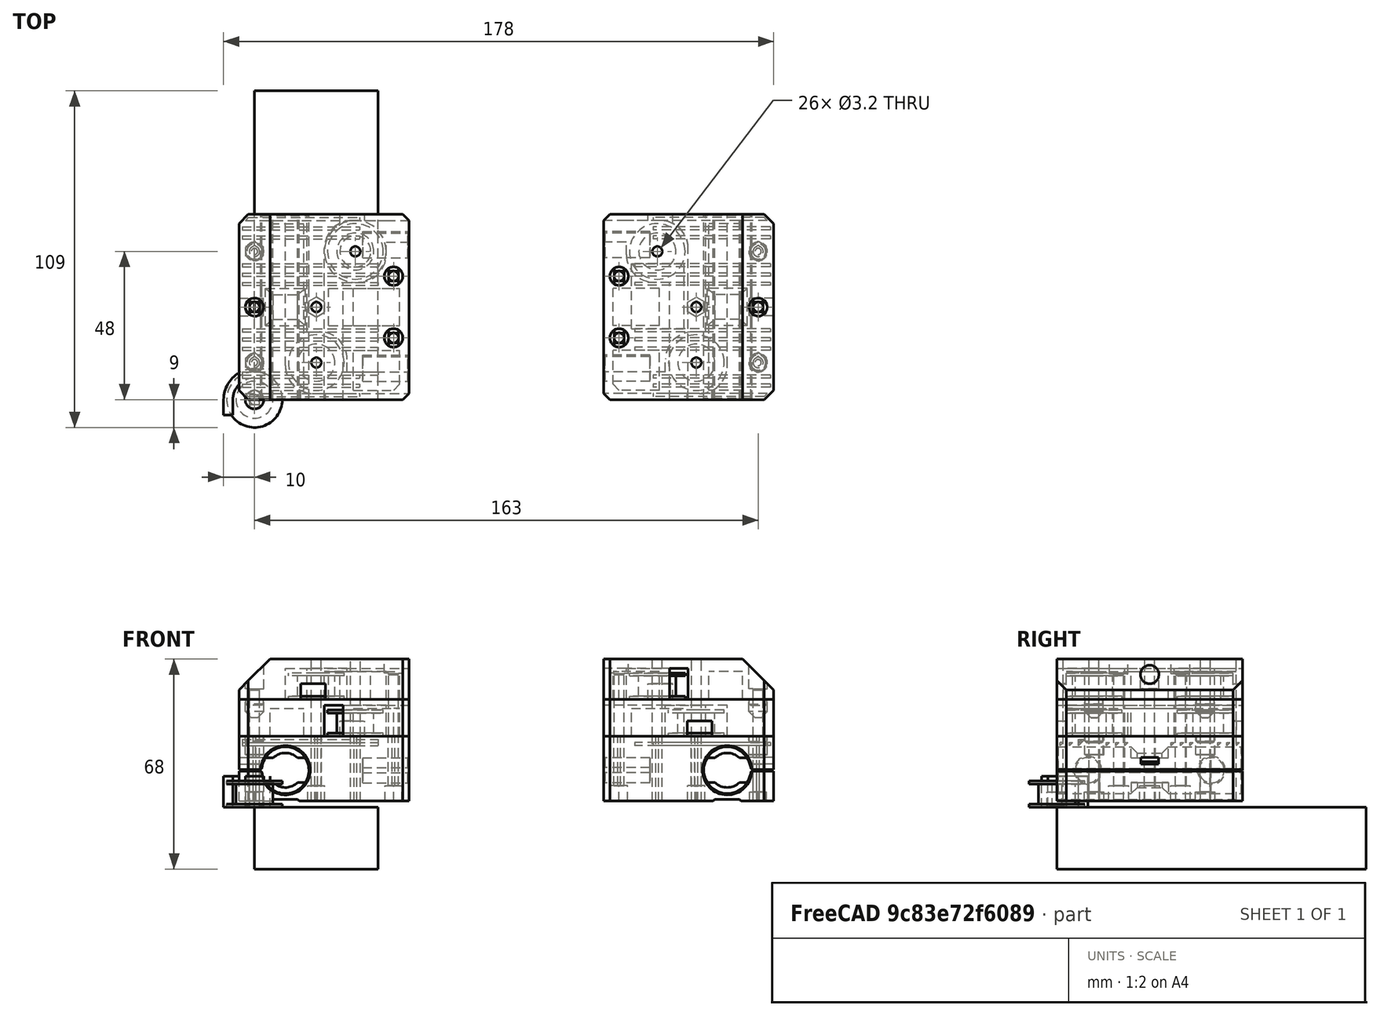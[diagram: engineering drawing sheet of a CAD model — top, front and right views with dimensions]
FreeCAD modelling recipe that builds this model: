
FCSTD DOCUMENT  (FreeCAD 0.18R14555 (Git shallow))
Label: Y-carrier
License: All rights reserved
LicenseURL: http://en.wikipedia.org/wiki/All_rights_reserved
objects: Part::Cylinder×59, Part::MultiFuse×41, Part::Box×39, Part::Cut×37, Part::Feature×29, Part::Chamfer×24, Part::MultiCommon×2, Part::Fillet×2
note: 233 computed .brp shape members not serialized (recipe doc carries the construction recipe); baked Part::Feature solids carry a one-line shape summary decoded from their .brp

FEATURE [Part::Box] Box  label="profile"
  AttacherType = Attacher::AttachEngine3D
  Height = 20
  Length = 40
  Placement = pos=(0,0,-20) rot=(0,0,1;0rad)
  Width = 100
FEATURE [Part::Cylinder] Cylinder  label="bushing-1"
  Angle = 360
  AttacherType = Attacher::AttachEngine3D
  Height = 24
  Placement = pos=(10,3e-15,12) rot=(-1,0,0;1.5708rad)
  Radius = 7.6
FEATURE [Part::Cylinder] Cylinder001  label="bushing-2"
  Angle = 360
  AttacherType = Attacher::AttachEngine3D
  Height = 24
  Placement = pos=(10,36,12) rot=(-1,0,0;1.5708rad)
  Radius = 7.6
FEATURE [Part::Cylinder] Cylinder002  label="rod"
  Angle = 360
  AttacherType = Attacher::AttachEngine3D
  Height = 100
  Placement = pos=(10,3e-15,12) rot=(-1,0,0;1.5708rad)
  Radius = 5.6
FEATURE [Part::Cylinder] Cylinder003  label="Cylinder"
  Angle = 360
  AttacherType = Attacher::AttachEngine3D
  Height = 30
  Placement = pos=(20,48,0) rot=(0,0,1;0rad)
  Radius = 1.6
FEATURE [Part::Cylinder] Cylinder004  label="Cylinder001-12.63"
  Angle = 360
  AttacherType = Attacher::AttachEngine3D
  Height = 30
  Placement = pos=(32.63,12,0) rot=(0,0,1;0rad)
  Radius = 1.6
FEATURE [Part::Box] Box001  label="Cube"
  AttacherType = Attacher::AttachEngine3D
  Height = 21
  Length = 55
  Placement = pos=(-5,0,2) rot=(0,0,1;0rad)
  Width = 60
FEATURE [Part::Cylinder] Cylinder005  label="Cylinder001"
  Angle = 360
  AttacherType = Attacher::AttachEngine3D
  Height = 1
  Radius = 9
FEATURE [Part::Cylinder] Cylinder006  label="Cylinder002"
  Angle = 360
  AttacherType = Attacher::AttachEngine3D
  Height = 1
  Placement = pos=(0,0,7.5) rot=(0,0,1;0rad)
  Radius = 9
FEATURE [Part::Cylinder] Cylinder007  label="Cylinder003"
  Angle = 360
  AttacherType = Attacher::AttachEngine3D
  Height = 8.5
  Radius = 6
FEATURE [Part::Cylinder] Cylinder008  label="Cylinder004"
  Angle = 360
  AttacherType = Attacher::AttachEngine3D
  Height = 8.5
  Radius = 1.6
FEATURE [Part::MultiFuse] Fusion
  Shapes = -> [Cylinder007,Cylinder006,Cylinder005]
FEATURE [Part::Cut] Cut  label="idler"
  Base = -> Fusion
  Tool = -> Cylinder008
FEATURE [Part::Feature] Cut001  label="idler001"
  Placement = pos=(20,12,35) rot=(0,0,1;0rad)
  shape: bbox 18 x 18 x 8.5 mm, 8 faces (baked)
FEATURE [Part::Feature] Cut002  label="idler002"
  Placement = pos=(32.63,48,23) rot=(0,0,1;0rad)
  shape: bbox 18 x 18 x 8.5 mm, 8 faces (baked)
FEATURE [Part::Cylinder] Cylinder009  label="Cylinder005"
  Angle = 360
  AttacherType = Attacher::AttachEngine3D
  Height = 20
  Placement = pos=(35,10,12) rot=(0,1,0;1.5708rad)
  Radius = 1
FEATURE [Part::Cylinder] Cylinder010  label="Cylinder006"
  Angle = 360
  AttacherType = Attacher::AttachEngine3D
  Height = 20
  Placement = pos=(35,50,12) rot=(0,1,0;1.5708rad)
  Radius = 1
FEATURE [Part::Cylinder] Cylinder011  label="Cylinder007"
  Angle = 360
  AttacherType = Attacher::AttachEngine3D
  Height = 30
  Placement = pos=(0,31.4,0) rot=(0,0,1;0rad)
  Radius = 0.5
FEATURE [Part::Cylinder] Cylinder012  label="Cylinder008"
  Angle = 360
  AttacherType = Attacher::AttachEngine3D
  Height = 30
  Placement = pos=(20,30,0) rot=(0,0,1;0rad)
  Radius = 1.65
FEATURE [Part::Cylinder] Cylinder014  label="Cylinder010"
  Angle = 360
  AttacherType = Attacher::AttachEngine3D
  Height = 30
  Placement = pos=(45,41.4,0) rot=(0,0,1;0rad)
  Radius = 0.5
FEATURE [Part::Cylinder] Cylinder015  label="Cylinder011"
  Angle = 360
  AttacherType = Attacher::AttachEngine3D
  Height = 6
  Placement = pos=(0,48,0) rot=(0,0,1;0rad)
  Radius = 3
FEATURE [Part::Cylinder] Cylinder016  label="Cylinder012"
  Angle = 360
  AttacherType = Attacher::AttachEngine3D
  Height = 6
  Placement = pos=(0,12,0) rot=(0,0,1;0rad)
  Radius = 3
FEATURE [Part::MultiFuse] Fusion001
  Shapes = -> [Cylinder002,Cylinder,Cylinder001]
FEATURE [Part::Box] Box002  label="Cube001"
  AttacherType = Attacher::AttachEngine3D
  Height = 0.5
  Length = 15
  Placement = pos=(-5,0,11.75) rot=(0,0,1;0rad)
  Width = 60
FEATURE [Part::Feature] Body001  label="hex-nut"
  shape: bbox 5.543 x 6.4 x 5 mm, 8 faces (baked)
FEATURE [Part::Feature] Body001001  label="hex-nut001"
  Placement = pos=(0,48,0) rot=(0,0,1;0rad)
  shape: bbox 5.543 x 6.4 x 5 mm, 8 faces (baked)
FEATURE [Part::Feature] Body001002  label="hex-nut002"
  Placement = pos=(0,12,0) rot=(0,0,1;0rad)
  shape: bbox 5.543 x 6.4 x 5 mm, 8 faces (baked)
FEATURE [Part::Cylinder] Cylinder017  label="Cylinder013"
  Angle = 360
  AttacherType = Attacher::AttachEngine3D
  Height = 30
  Placement = pos=(0,48,0) rot=(0,0,1;0rad)
  Radius = 0.5
FEATURE [Part::Cylinder] Cylinder018  label="Cylinder014"
  Angle = 360
  AttacherType = Attacher::AttachEngine3D
  Height = 30
  Placement = pos=(0,12,0) rot=(0,0,1;0rad)
  Radius = 0.5
FEATURE [Part::Cylinder] Cylinder019  label="Cylinder015"
  Angle = 360
  AttacherType = Attacher::AttachEngine3D
  Height = 30
  Placement = pos=(0,12,0) rot=(0,0,1;0rad)
  Radius = 1.65
FEATURE [Part::Cylinder] Cylinder020  label="Cylinder016"
  Angle = 360
  AttacherType = Attacher::AttachEngine3D
  Height = 30
  Placement = pos=(0,48,0) rot=(0,0,1;0rad)
  Radius = 1.65
FEATURE [Part::MultiFuse] Fusion003002
  Placement = pos=(0,1.4,0) rot=(0,0,1;0rad)
  Shapes = -> [Cylinder018,Cylinder017]
FEATURE [Part::Cylinder] Cylinder021  label="Cylinder017"
  Angle = 360
  AttacherType = Attacher::AttachEngine3D
  Height = 6
  Placement = pos=(0,12,0) rot=(0,0,1;0rad)
  Radius = 0.5
FEATURE [Part::Cylinder] Cylinder022  label="Cylinder018"
  Angle = 360
  AttacherType = Attacher::AttachEngine3D
  Height = 6
  Placement = pos=(0,48,0) rot=(0,0,1;0rad)
  Radius = 0.5
FEATURE [Part::Box] Box003  label="Cube002"
  AttacherType = Attacher::AttachEngine3D
  Height = 2.2
  Length = 8.8
  Placement = pos=(-5.9,27.1,14) rot=(0,0,1;0rad)
  Width = 5.8
FEATURE [Part::Feature] Body001003  label="hex-nut003"
  Placement = pos=(20,30,2) rot=(0,0,1;0rad)
  shape: bbox 5.543 x 6.4 x 5 mm, 8 faces (baked)
FEATURE [Part::Feature] Body001004  label="hex-nut004"
  Placement = pos=(45,40,2) rot=(0,0,1;0rad)
  shape: bbox 5.543 x 6.4 x 5 mm, 8 faces (baked)
FEATURE [Part::Cylinder] Cylinder023  label="Cylinder019"
  Angle = 360
  AttacherType = Attacher::AttachEngine3D
  Height = 30
  Placement = pos=(45,21.4,0) rot=(0,0,1;0rad)
  Radius = 0.5
FEATURE [Part::Feature] Body001005  label="hex-nut005"
  Placement = pos=(45,20,2) rot=(0,0,1;0rad)
  shape: bbox 5.543 x 6.4 x 5 mm, 8 faces (baked)
FEATURE [Part::Cylinder] Cylinder024  label="Cylinder020"
  Angle = 360
  AttacherType = Attacher::AttachEngine3D
  Height = 20
  Placement = pos=(35,10,12) rot=(0,1,0;1.5708rad)
  Radius = 4.075
FEATURE [Part::Cylinder] Cylinder025  label="Cylinder021"
  Angle = 360
  AttacherType = Attacher::AttachEngine3D
  Height = 20
  Placement = pos=(35,50,12) rot=(0,1,0;1.5708rad)
  Radius = 4.075
FEATURE [Part::MultiFuse] Fusion003006
  Shapes = -> [Cylinder024,Cylinder025]
FEATURE [Part::Cylinder] Cylinder026  label="Cylinder022"
  Angle = 360
  AttacherType = Attacher::AttachEngine3D
  Height = 30
  Placement = pos=(0,30,0) rot=(0,0,1;0rad)
  Radius = 1.65
FEATURE [Part::Cylinder] Cylinder027  label="Cylinder023"
  Angle = 360
  AttacherType = Attacher::AttachEngine3D
  Height = 30
  Placement = pos=(45,20,0) rot=(0,0,1;0rad)
  Radius = 1.65
FEATURE [Part::Cylinder] Cylinder028  label="Cylinder024"
  Angle = 360
  AttacherType = Attacher::AttachEngine3D
  Height = 30
  Placement = pos=(45,40,0) rot=(0,0,1;0rad)
  Radius = 1.65
FEATURE [Part::MultiFuse] Fusion003008
  Shapes = -> [Cylinder027,Cylinder023]
FEATURE [Part::MultiFuse] Fusion003009
  Shapes = -> [Cylinder014,Cylinder028]
FEATURE [Part::MultiFuse] Fusion003010
  Shapes = -> [Cylinder011,Cylinder026]
FEATURE [Part::Cylinder] Cylinder029  label="Cylinder025"
  Angle = 360
  AttacherType = Attacher::AttachEngine3D
  Height = 30
  Placement = pos=(20,31.4,0) rot=(0,0,1;0rad)
  Radius = 0.5
FEATURE [Part::MultiFuse] Fusion003011
  Shapes = -> [Cylinder012,Cylinder029]
FEATURE [Part::MultiFuse] Fusion003012
  Placement = pos=(0,3.4,0) rot=(0,0,1;0rad)
  Shapes = -> [Cylinder009,Cylinder010]
FEATURE [Part::Cylinder] Cylinder030  label="Cylinder001-12.064"
  Angle = 360
  AttacherType = Attacher::AttachEngine3D
  Height = 30
  Placement = pos=(32.63,13.3,0) rot=(0,0,1;0rad)
  Radius = 0.5
FEATURE [Part::Cylinder] Cylinder031  label="Cylinder026"
  Angle = 360
  AttacherType = Attacher::AttachEngine3D
  Height = 30
  Placement = pos=(20,49.3,0) rot=(0,0,1;0rad)
  Radius = 0.5
FEATURE [Part::MultiFuse] Fusion003015
  Shapes = -> [Fusion003011,Body001003]
FEATURE [Part::MultiFuse] Fusion003016
  Shapes = -> [Fusion003008,Body001005]
FEATURE [Part::MultiFuse] Fusion003017
  Shapes = -> [Fusion003009,Body001004]
FEATURE [Part::Box] Box004  label="Cube003"
  AttacherType = Attacher::AttachEngine3D
  Height = 3
  Length = 10
  Placement = pos=(5,0,0) rot=(0,0,1;0rad)
  Width = 60
FEATURE [Part::Chamfer] Chamfer003
  Base = -> Box004
  Edges = 2 edges r=1: [Edge2,Edge6]
  Placement = pos=(0,0,-0.5) rot=(0,0,1;0rad)
FEATURE [Part::Cylinder] Cylinder032  label="Cylinder027"
  Angle = 360
  AttacherType = Attacher::AttachEngine3D
  Height = 12
  Placement = pos=(10,24,12) rot=(-1,0,0;1.5708rad)
  Radius = 7.6
FEATURE [Part::Box] Box005  label="Cube004"
  AttacherType = Attacher::AttachEngine3D
  Height = 8
  Length = 16
  Placement = pos=(2,24,8) rot=(0,0,1;0rad)
  Width = 12
FEATURE [Part::MultiCommon] Common
  Shapes = -> [Cylinder032,Box005]
FEATURE [Part::Cut] Cut003
  Base = -> Box001
  Tool = -> Fusion001
FEATURE [Part::MultiFuse] Fusion003019
  Placement = pos=(0,2.7,0) rot=(0,0,1;0rad)
  Shapes = -> [Cylinder022,Cylinder021]
FEATURE [Part::MultiFuse] Fusion003020
  Placement = pos=(0,0,17) rot=(0,0,1;0rad)
  Shapes = -> [Fusion003019,Cylinder016,Cylinder015]
FEATURE [Part::MultiFuse] Fusion003021
  Shapes = -> [Body001001,Cylinder020,Fusion003020,Body001002,Cylinder019]
FEATURE [Part::MultiFuse] Fusion003022
  Shapes = -> [Fusion003002,Fusion003021]
FEATURE [Part::Box] Box007  label="Cube006"
  AttacherType = Attacher::AttachEngine3D
  Height = 2
  Length = 44
  Placement = pos=(-4,7,21) rot=(0,0,1;0rad)
  Width = 1
FEATURE [Part::Box] Box006  label="Cube005"
  AttacherType = Attacher::AttachEngine3D
  Height = 2
  Length = 44
  Placement = pos=(-4,7,21) rot=(0,0,1;0rad)
  Width = 2
FEATURE [Part::Box] Box008  label="Cube007"
  AttacherType = Attacher::AttachEngine3D
  Height = 1
  Length = 44
  Placement = pos=(-4,8,22) rot=(0,0,1;0rad)
  Width = 1
FEATURE [Part::Feature] Cut013001  label="select-infill-short"
  Placement = pos=(0,-1,0) rot=(0,0,1;0rad)
  shape: bbox 38 x 1 x 1 mm, 5 faces (baked)
FEATURE [Part::Chamfer] Chamfer006
  Base = -> Box006
  Edges = 1 edges r=1: [Edge11]
FEATURE [Part::Cut] Cut013002
  Base = -> Chamfer006
  Tool = -> Box007
FEATURE [Part::Cut] Cut013003  label="select-infill-long"
  Base = -> Cut013002
  Tool = -> Box008
FEATURE [Part::Feature] Cut013001001  label="select-infill-short001"
  shape: bbox 38 x 1 x 1 mm, 5 faces (baked)
FEATURE [Part::Feature] Cut013003001  label="select-infill-long001"
  Placement = pos=(0,8,0) rot=(0,0,1;0rad)
  shape: bbox 44 x 1 x 1 mm, 5 faces (baked)
FEATURE [Part::Feature] Cut013003002  label="select-infill-long002"
  Placement = pos=(0,11,0) rot=(0,0,1;0rad)
  shape: bbox 44 x 1 x 1 mm, 5 faces (baked)
FEATURE [Part::Feature] Cut013003003  label="select-infill-long003"
  Placement = pos=(0,14,0) rot=(0,0,1;0rad)
  shape: bbox 44 x 1 x 1 mm, 5 faces (baked)
FEATURE [Part::Feature] Cut013003004  label="select-infill-short002"
  Placement = pos=(0,-3,0) rot=(0,0,1;0rad)
  shape: bbox 38 x 1 x 1 mm, 5 faces (baked)
FEATURE [Part::Feature] Cut013003005  label="select-infill-short003"
  Placement = pos=(0,-6,0) rot=(0,0,1;0rad)
  shape: bbox 38 x 1 x 1 mm, 5 faces (baked)
FEATURE [Part::MultiFuse] Fusion003024
  Placement = pos=(0,0,-1) rot=(0,0,1;0rad)
  Shapes = -> [Cut013003001,Cut013003002,Cut013003003]
FEATURE [Part::MultiFuse] Fusion003025
  Placement = pos=(0,0,-1) rot=(0,0,1;0rad)
  Shapes = -> [Cut013003005,Cut013003004,Cut013001001]
FEATURE [Part::Feature] Fusion003024001  label="Fusion003026"
  Placement = pos=(0,21,-1) rot=(0,0,1;0rad)
  shape: bbox 44 x 7 x 1 mm, 15 faces, 3 solids (baked)
FEATURE [Part::Feature] Fusion003025001  label="Fusion003027"
  Placement = pos=(0,51,-1) rot=(0,0,1;0rad)
  shape: bbox 38 x 7 x 1 mm, 15 faces, 3 solids (baked)
FEATURE [Part::Box] Box009  label="Cube008"
  AttacherType = Attacher::AttachEngine3D
  Height = 10
  Length = 3
  Placement = pos=(-5,0,13) rot=(0,0,1;0rad)
  Width = 3
FEATURE [Part::Box] Box010  label="Cube009"
  AttacherType = Attacher::AttachEngine3D
  Height = 10
  Length = 3
  Placement = pos=(-5,57,13) rot=(0,0,1;0rad)
  Width = 3
FEATURE [Part::Chamfer] Chamfer007
  Base = -> Box010
  Edges = 1 edges r=2: [Edge5]
FEATURE [Part::Cut] Cut013003006
  Base = -> Fusion003025001
  Tool = -> Chamfer007
FEATURE [Part::Chamfer] Chamfer008
  Base = -> Box009
  Edges = 1 edges r=2: [Edge7]
FEATURE [Part::Cut] Cut013003007
  Base = -> Fusion003025
  Tool = -> Chamfer008
FEATURE [Part::MultiFuse] Fusion003025002
  Shapes = -> [Cut013003007,Fusion003024001,Cut013003006,Fusion003024]
FEATURE [Part::Chamfer] Chamfer
  Base = -> Cut003
  Edges = 2 edges r=1.99: [Edge19,Edge20]
FEATURE [Part::Cut] Cut013003008
  Base = -> Chamfer
  Tool = -> Common
FEATURE [Part::Cut] Cut013003009
  Base = -> Cut013003008
  Tool = -> Box002
FEATURE [Part::Cut] Cut013003010
  Base = -> Cut013003009
  Tool = -> Fusion003022
FEATURE [Part::MultiFuse] Fusion003025003
  Placement = pos=(-12.63,0,0) rot=(0,0,1;0rad)
  Shapes = -> [Cylinder030,Cylinder004]
FEATURE [Part::MultiFuse] Fusion003025004
  Placement = pos=(12.63,0,0) rot=(0,0,1;0rad)
  Shapes = -> [Cylinder031,Cylinder003]
FEATURE [Part::MultiFuse] Fusion003025005
  Shapes = -> [Fusion003025004,Fusion003025003,Fusion003015,Fusion003017,Fusion003016]
FEATURE [Part::MultiFuse] Fusion003025006
  Shapes = -> [Fusion003010,Box003]
FEATURE [Part::MultiFuse] Fusion003025007
  Shapes = -> [Fusion003025006,Fusion003025005]
FEATURE [Part::Cut] Cut013003011
  Base = -> Cut013003010
  Tool = -> Fusion003025007
FEATURE [Part::Cut] Cut013003012
  Base = -> Cut013003011
  Tool = -> Chamfer003
FEATURE [Part::Cut] Cut013003013
  Base = -> Cut013003012
  Tool = -> Fusion003006
FEATURE [Part::Chamfer] Chamfer009
  Base = -> Cut013003013
  Edges = 10 edges r=0.4: [Edge15,Edge16,Edge26,Edge27,Edge35,Edge57,Edge60,Edge84,Edge182,Edge183]
FEATURE [Part::Cut] Cut013003014
  Base = -> Chamfer009
  Tool = -> Fusion003012
FEATURE [Part::Chamfer] Chamfer010
  Base = -> Cut013003014
  Edges = 4 edges r=3: [Edge43,Edge47,Edge120,Edge152]
FEATURE [Part::Chamfer] Chamfer011
  Base = -> Chamfer010
  Edges = 2 edges r=2: [Edge6,Edge67]
FEATURE [Part::Cut] Cut013003015  label="Y-bottom-L"
  Base = -> Chamfer011
  Tool = -> Fusion003025002
FEATURE [Part::Box] Box011  label="Cube010"
  AttacherType = Attacher::AttachEngine3D
  Height = 12
  Length = 55
  Placement = pos=(-5,0,23) rot=(0,0,1;0rad)
  Width = 60
FEATURE [Part::Box] Box012  label="Cube011"
  AttacherType = Attacher::AttachEngine3D
  Height = 10
  Length = 20
  Placement = pos=(22.63,38,23) rot=(0,0,1;0rad)
  Width = 20
FEATURE [Part::Fillet] Fillet
  Base = -> Box012
  Edges = 2 edges r=9: [Edge3,Edge5]
FEATURE [Part::Box] Box013  label="Cube012"
  AttacherType = Attacher::AttachEngine3D
  Height = 10
  Length = 6
  Placement = pos=(22.63,0,23) rot=(0,0,1;0rad)
  Width = 38
FEATURE [Part::Box] Box014  label="Cube013"
  AttacherType = Attacher::AttachEngine3D
  Height = 10
  Length = 9
  Placement = pos=(42,51,23) rot=(0,0,1;0rad)
  Width = 7
FEATURE [Part::Cylinder] Cylinder033  label="Cylinder028"
  Angle = 360
  AttacherType = Attacher::AttachEngine3D
  Height = 2
  Placement = pos=(0,12,22) rot=(0,0,1;0rad)
  Radius = 2.9
FEATURE [Part::Cylinder] Cylinder035  label="Cylinder030"
  Angle = 360
  AttacherType = Attacher::AttachEngine3D
  Height = 20
  Placement = pos=(0,30,22) rot=(0,0,1;0rad)
  Radius = 1.6
FEATURE [Part::Cylinder] Cylinder036  label="Cylinder031"
  Angle = 360
  AttacherType = Attacher::AttachEngine3D
  Height = 2
  Placement = pos=(0,48,22) rot=(0,0,1;0rad)
  Radius = 2.9
FEATURE [Part::Cylinder] Cylinder037  label="Cylinder032"
  Angle = 360
  AttacherType = Attacher::AttachEngine3D
  Height = 20
  Placement = pos=(20,12,22) rot=(0,0,1;0rad)
  Radius = 1.6
FEATURE [Part::Cylinder] Cylinder038  label="Cylinder033"
  Angle = 360
  AttacherType = Attacher::AttachEngine3D
  Height = 20
  Placement = pos=(20,30,22) rot=(0,0,1;0rad)
  Radius = 1.6
FEATURE [Part::Cylinder] Cylinder039  label="Cylinder034"
  Angle = 360
  AttacherType = Attacher::AttachEngine3D
  Height = 20
  Placement = pos=(32.63,48,22) rot=(0,0,1;0rad)
  Radius = 1.6
FEATURE [Part::Cylinder] Cylinder040  label="Cylinder035"
  Angle = 360
  AttacherType = Attacher::AttachEngine3D
  Height = 20
  Placement = pos=(45,40,22) rot=(0,0,1;0rad)
  Radius = 1.6
FEATURE [Part::Cylinder] Cylinder041  label="Cylinder036"
  Angle = 360
  AttacherType = Attacher::AttachEngine3D
  Height = 20
  Placement = pos=(45,20,22) rot=(0,0,1;0rad)
  Radius = 1.6
FEATURE [Part::MultiFuse] Fusion003025009
  Shapes = -> [Cylinder035,Cylinder038,Cylinder037,Cylinder041,Cylinder040,Cylinder039]
FEATURE [Part::Cylinder] Cylinder042  label="Cylinder037"
  Angle = 360
  AttacherType = Attacher::AttachEngine3D
  Height = 6
  Placement = pos=(0,12,35) rot=(0,0,1;0rad)
  Radius = 3
FEATURE [Part::Cylinder] Cylinder043  label="Cylinder038"
  Angle = 360
  AttacherType = Attacher::AttachEngine3D
  Height = 6
  Placement = pos=(0,48,35) rot=(0,0,1;0rad)
  Radius = 3
FEATURE [Part::Chamfer] Chamfer016
  Base = -> Cylinder043
  Edges = 1 edges r=2: [Edge3]
FEATURE [Part::Chamfer] Chamfer017
  Base = -> Cylinder042
  Edges = 1 edges r=2: [Edge3]
FEATURE [Part::MultiFuse] Fusion003025012
  Placement = pos=(0,0,-6) rot=(0,0,1;0rad)
  Shapes = -> [Chamfer016,Chamfer017]
FEATURE [Part::Box] Box015  label="Cube014"
  AttacherType = Attacher::AttachEngine3D
  Height = 9
  Length = 11
  Placement = pos=(5,3,23) rot=(0,0,1;0rad)
  Width = 54
FEATURE [Part::Box] Box016  label="Cube015"
  AttacherType = Attacher::AttachEngine3D
  Height = 9
  Length = 15
  Placement = pos=(32,3,23) rot=(0,0,1;0rad)
  Width = 13
FEATURE [Part::Box] Box017  label="Cube016"
  AttacherType = Attacher::AttachEngine3D
  Height = 9
  Length = 15
  Placement = pos=(32,24,23) rot=(0,0,1;0rad)
  Width = 12
FEATURE [Part::Box] Box018  label="Cube017"
  AttacherType = Attacher::AttachEngine3D
  Height = 10
  Length = 7
  Placement = pos=(10,22,35) rot=(0,0,1;0rad)
  Width = 38
FEATURE [Part::Box] Box019  label="Cube018"
  AttacherType = Attacher::AttachEngine3D
  Height = 10
  Length = 20
  Placement = pos=(10,2,35) rot=(0,0,1;0rad)
  Width = 20
FEATURE [Part::Fillet] Fillet001
  Base = -> Box019
  Edges = 2 edges r=9: [Edge1,Edge7]
FEATURE [Part::Box] Box020  label="Cube019"
  AttacherType = Attacher::AttachEngine3D
  Height = 13
  Length = 55
  Placement = pos=(-5,0,35) rot=(0,0,1;0rad)
  Width = 60
FEATURE [Part::Box] Box021  label="Cube020"
  AttacherType = Attacher::AttachEngine3D
  Height = 10
  Length = 20
  Placement = pos=(30,2,35) rot=(0,0,1;0rad)
  Width = 7
FEATURE [Part::MultiFuse] Fusion003025014
  Shapes = -> [Box018,Fillet001,Box021]
FEATURE [Part::Cut] Cut013003020
  Base = -> Box020
  Tool = -> Fusion003025014
FEATURE [Part::MultiFuse] Fusion003025015
  Shapes = -> [Box013,Fillet,Box014]
FEATURE [Part::Cut] Cut013003021
  Base = -> Box011
  Tool = -> Fusion003025009
FEATURE [Part::Cut] Cut013003022
  Base = -> Cut013003021
  Tool = -> Fusion003025015
FEATURE [Part::Cut] Cut013003023
  Base = -> Cut013003022
  Tool = -> Fusion003025012
FEATURE [Part::Chamfer] Chamfer018
  Base = -> Box016
  Edges = 1 edges r=2: [Edge5]
FEATURE [Part::MultiFuse] Fusion003025016
  Shapes = -> [Box017,Chamfer018,Box015]
FEATURE [Part::Cylinder] Cylinder044  label="Cylinder039"
  Angle = 360
  AttacherType = Attacher::AttachEngine3D
  Height = 2
  Placement = pos=(0,12,35) rot=(0,0,1;0rad)
  Radius = 2.85
FEATURE [Part::Cylinder] Cylinder045  label="Cylinder040"
  Angle = 360
  AttacherType = Attacher::AttachEngine3D
  Height = 2
  Placement = pos=(0,48,35) rot=(0,0,1;0rad)
  Radius = 2.85
FEATURE [Part::Chamfer] Chamfer024
  Base = -> Cut013003020
  Edges = 1 edges r=1.99: [Edge6]
FEATURE [Part::Chamfer] Chamfer025
  Base = -> Chamfer024
  Edges = 1 edges r=2: [Edge20]
FEATURE [Part::Chamfer] Chamfer026
  Base = -> Chamfer025
  Edges = 2 edges r=3: [Edge21,Edge25]
FEATURE [Part::Cylinder] Cylinder046  label="Cylinder041"
  Angle = 360
  AttacherType = Attacher::AttachEngine3D
  Height = 13
  Placement = pos=(0,30,35) rot=(0,0,1;0rad)
  Radius = 1.6
FEATURE [Part::Cylinder] Cylinder047  label="Cylinder042"
  Angle = 360
  AttacherType = Attacher::AttachEngine3D
  Height = 13
  Placement = pos=(20,12,35) rot=(0,0,1;0rad)
  Radius = 1.6
FEATURE [Part::Cylinder] Cylinder048  label="Cylinder043"
  Angle = 360
  AttacherType = Attacher::AttachEngine3D
  Height = 13
  Placement = pos=(20,30,35) rot=(0,0,1;0rad)
  Radius = 1.6
FEATURE [Part::Cylinder] Cylinder049  label="Cylinder044"
  Angle = 360
  AttacherType = Attacher::AttachEngine3D
  Height = 13
  Placement = pos=(45,40,35) rot=(0,0,1;0rad)
  Radius = 1.6
FEATURE [Part::Cylinder] Cylinder050  label="Cylinder045"
  Angle = 360
  AttacherType = Attacher::AttachEngine3D
  Height = 13
  Placement = pos=(45,20,35) rot=(0,0,1;0rad)
  Radius = 1.6
FEATURE [Part::Cylinder] Cylinder051  label="Cylinder046"
  Angle = 360
  AttacherType = Attacher::AttachEngine3D
  Height = 13
  Placement = pos=(32.63,48,35) rot=(0,0,1;0rad)
  Radius = 1.6
FEATURE [Part::MultiFuse] Fusion003025019
  Shapes = -> [Cylinder046,Cylinder049,Cylinder047,Cylinder050,Cylinder048,Cylinder051]
FEATURE [Part::Cut] Cut013003025
  Base = -> Chamfer026
  Tool = -> Fusion003025019
FEATURE [Part::Cut] Cut013003026
  Base = -> Cut013003023
  Tool = -> Fusion003025016
FEATURE [Part::MultiFuse] Fusion003025021
  Placement = pos=(0,0,-1) rot=(0,0,1;0rad)
  Shapes = -> [Cylinder033,Cylinder036]
FEATURE [Part::Chamfer] Chamfer027
  Base = -> Fusion003025021
  Edges = 2 edges r=0.4: [Edge3,Edge6]
FEATURE [Part::Chamfer] Chamfer028
  Base = -> Cut013003026
  Edges = 1 edges r=1.99: [Edge23]
FEATURE [Part::Chamfer] Chamfer029
  Base = -> Chamfer028
  Edges = 1 edges r=2: [Edge21]
FEATURE [Part::Chamfer] Chamfer030
  Base = -> Chamfer029
  Edges = 2 edges r=3: [Edge29,Edge33]
FEATURE [Part::MultiFuse] Fusion003025022  label="Y-mid-L"
  Shapes = -> [Chamfer030,Chamfer027]
FEATURE [Part::Feature] Part__Mirroring001  label="Y-top-R-tmp"
  Placement = pos=(163,0,12) rot=(0,0,1;0rad)
  shape: bbox 55 x 60 x 14 mm, 60 faces (baked)
FEATURE [Part::Feature] Part__Mirroring002  label="Y-bottom-R"
  Placement = pos=(163,0,0) rot=(0,0,1;0rad)
  shape: bbox 55 x 60 x 21 mm, 213 faces (baked)
FEATURE [Part::Chamfer] Chamfer031
  Base = -> Cylinder045
  Edges = 1 edges r=0.4: [Edge3]
FEATURE [Part::Chamfer] Chamfer032
  Base = -> Cylinder044
  Edges = 1 edges r=0.4: [Edge3]
FEATURE [Part::MultiFuse] Fusion003025020002
  Placement = pos=(0,0,-2) rot=(0,0,1;0rad)
  Shapes = -> [Chamfer031,Chamfer032]
FEATURE [Part::MultiFuse] Fusion003025020003
  Shapes = -> [Cut013003025,Fusion003025020002]
FEATURE [Part::Feature] Part__Mirroring003  label="Y-mid-R-tmp"
  Placement = pos=(163,0,-12) rot=(0,0,1;0rad)
  shape: bbox 55 x 60 x 14 mm, 36 faces (baked)
FEATURE [Part::Cylinder] Cylinder052  label="Cylinder047"
  Angle = 360
  AttacherType = Attacher::AttachEngine3D
  Height = 6
  Placement = pos=(163,12,29) rot=(0,0,1;0rad)
  Radius = 3
FEATURE [Part::Cylinder] Cylinder053  label="Cylinder048"
  Angle = 360
  AttacherType = Attacher::AttachEngine3D
  Height = 6
  Placement = pos=(163,48,29) rot=(0,0,1;0rad)
  Radius = 3
FEATURE [Part::Chamfer] Chamfer033
  Base = -> Cylinder052
  Edges = 1 edges r=2: [Edge3]
FEATURE [Part::Chamfer] Chamfer034
  Base = -> Cylinder053
  Edges = 1 edges r=2: [Edge3]
FEATURE [Part::MultiFuse] Fusion003025020004
  Shapes = -> [Chamfer033,Chamfer034]
FEATURE [Part::Cut] Cut013003027  label="fdg"
  Base = -> Part__Mirroring003
  Tool = -> Fusion003025020004
FEATURE [Part::Feature] Cut013003028  label="idler003"
  Placement = pos=(143,12,23) rot=(0,0,1;0rad)
  shape: bbox 18 x 18 x 8.5 mm, 8 faces (baked)
FEATURE [Part::Feature] Cut013003029  label="idler004"
  Placement = pos=(130.37,48,35) rot=(0,0,1;0rad)
  shape: bbox 18 x 18 x 8.5 mm, 8 faces (baked)
FEATURE [Part::Cylinder] Cylinder054  label="Cylinder049"
  Angle = 360
  AttacherType = Attacher::AttachEngine3D
  Height = 6
  Placement = pos=(163,12,41) rot=(0,0,1;0rad)
  Radius = 3.1
FEATURE [Part::Cylinder] Cylinder055  label="Cylinder050"
  Angle = 360
  AttacherType = Attacher::AttachEngine3D
  Height = 6
  Placement = pos=(163,48,41) rot=(0,0,1;0rad)
  Radius = 3.1
FEATURE [Part::MultiFuse] Fusion003025020005
  Shapes = -> [Part__Mirroring001,Cylinder055,Cylinder054]
FEATURE [Part::Box] Box022  label="Cube021"
  AttacherType = Attacher::AttachEngine3D
  Height = 1
  Length = 55
  Placement = pos=(113,0,46) rot=(0,0,1;0rad)
  Width = 60
FEATURE [Part::Feature] Fusion003025020005001  label="Fusion003025020006"
  shape: bbox 55 x 60 x 14 mm, 48 faces (baked)
FEATURE [Part::MultiCommon] Common001
  Placement = pos=(0,0,1) rot=(0,0,1;0rad)
  Shapes = -> [Box022,Fusion003025020005001]
FEATURE [Part::MultiFuse] Fusion003025020005002  label="T-top-R-tmp2"
  Shapes = -> [Fusion003025020005,Common001]
FEATURE [Part::Box] Box023  label="Cube022"
  AttacherType = Attacher::AttachEngine3D
  Height = 20
  Length = 20
  Placement = pos=(-5,0,38) rot=(0,0,1;0rad)
  Width = 60
FEATURE [Part::Chamfer] Chamfer035
  Base = -> Box023
  Edges = 1 edges r=10: [Edge8]
  Placement = pos=(-10,0,0) rot=(0,0,1;0rad)
FEATURE [Part::Cut] Cut013003030
  Base = -> Fusion003025020003
  Tool = -> Chamfer035
FEATURE [Part::Box] Box025  label="Cube024"
  AttacherType = Attacher::AttachEngine3D
  Height = 20
  Length = 20
  Placement = pos=(175,0,0) rot=(0,0,1;0rad)
  Width = 60
FEATURE [Part::Chamfer] Chamfer036
  Base = -> Box025
  Edges = 1 edges r=10: [Edge4]
  Placement = pos=(-17,0,38) rot=(0,0,1;0rad)
FEATURE [Part::Cut] Cut013003031
  Base = -> Fusion003025020005002
  Tool = -> Chamfer036
FEATURE [Part::Cylinder] Cylinder056  label="Cylinder051"
  Angle = 360
  AttacherType = Attacher::AttachEngine3D
  Height = 10
  Radius = 3
FEATURE [Part::Box] Box026  label="Cube025"
  AttacherType = Attacher::AttachEngine3D
  Height = 0.4
  Length = 10
  Placement = pos=(1.6,-5,0) rot=(0,0,1;0rad)
  Width = 10
FEATURE [Part::Box] Box027  label="Cube026"
  AttacherType = Attacher::AttachEngine3D
  Height = 0.4
  Length = 10
  Placement = pos=(-11.6,-5,0) rot=(0,0,1;0rad)
  Width = 10
FEATURE [Part::Box] Box028  label="Cube027"
  AttacherType = Attacher::AttachEngine3D
  Height = 0.2
  Length = 10
  Placement = pos=(-5,1.6,0) rot=(0,0,1;0rad)
  Width = 10
FEATURE [Part::Box] Box029  label="Cube028"
  AttacherType = Attacher::AttachEngine3D
  Height = 0.2
  Length = 10
  Placement = pos=(-5,-11.6,0) rot=(0,0,1;0rad)
  Width = 10
FEATURE [Part::MultiFuse] Fusion003025020005003
  Shapes = -> [Box027,Box026,Box028,Box029]
FEATURE [Part::Cut] Cut013003032  label="m3-slot"
  Base = -> Cylinder056
  Tool = -> Fusion003025020005003
FEATURE [Part::Feature] Cut013003032001  label="m3-slot001"
  Placement = pos=(0,30,38) rot=(0,0,1;0rad)
  shape: bbox 6 x 6 x 10 mm, 11 faces (baked)
FEATURE [Part::Feature] Cut013003032002  label="m3-slot002"
  Placement = pos=(163,30,38) rot=(0,0,1;0rad)
  shape: bbox 6 x 6 x 10 mm, 11 faces (baked)
FEATURE [Part::Feature] Cut013003032003  label="m3-slot003"
  Placement = pos=(45,40,43) rot=(0,0,1;0rad)
  shape: bbox 6 x 6 x 10 mm, 11 faces (baked)
FEATURE [Part::Feature] Cut013003032004  label="m3-slot004"
  Placement = pos=(45,20,43) rot=(0,0,1;0rad)
  shape: bbox 6 x 6 x 10 mm, 11 faces (baked)
FEATURE [Part::Feature] Cut013003032005  label="m3-slot005"
  Placement = pos=(118,40,43) rot=(0,0,1;0rad)
  shape: bbox 6 x 6 x 10 mm, 11 faces (baked)
FEATURE [Part::Feature] Cut013003032006  label="m3-slot006"
  Placement = pos=(118,20,43) rot=(0,0,1;0rad)
  shape: bbox 6 x 6 x 10 mm, 11 faces (baked)
FEATURE [Part::MultiFuse] Fusion003025020005004
  Shapes = -> [Cut013003032001,Cut013003032003,Cut013003032004]
FEATURE [Part::Cut] Cut013003032007
  Base = -> Cut013003030
  Tool = -> Fusion003025020005004
FEATURE [Part::MultiFuse] Fusion003025020005005
  Shapes = -> [Cut013003032006,Cut013003032005,Cut013003032002]
FEATURE [Part::Cut] Cut013003032008
  Base = -> Cut013003031
  Tool = -> Fusion003025020005005
FEATURE [Part::Box] Box030  label="Cube029"
  AttacherType = Attacher::AttachEngine3D
  Height = 9
  Length = 17
  Placement = pos=(122,23,23) rot=(0,0,1;0rad)
  Width = 21
FEATURE [Part::Cut] Cut013003032009  label="Y-mid-R"
  Base = -> Cut013003027
  Tool = -> Box030
FEATURE [Part::Box] Box031  label="Cube030"
  AttacherType = Attacher::AttachEngine3D
  Height = 9
  Length = 23
  Placement = pos=(24,24,35) rot=(0,0,1;0rad)
  Width = 12
FEATURE [Part::Cylinder] Cylinder057  label="Cylinder052"
  Angle = 360
  AttacherType = Attacher::AttachEngine3D
  Height = 9
  Placement = pos=(32.63,48,35) rot=(0,0,1;0rad)
  Radius = 5
FEATURE [Part::Cylinder] Cylinder058  label="Cylinder053"
  Angle = 360
  AttacherType = Attacher::AttachEngine3D
  Height = 9
  Placement = pos=(32.63,48,35) rot=(0,0,1;0rad)
  Radius = 10
FEATURE [Part::Cut] Cut013003032010
  Base = -> Cylinder058
  Tool = -> Cylinder057
FEATURE [Part::Cut] Cut013003032011
  Base = -> Cut013003032007
  Tool = -> Cut013003032010
FEATURE [Part::Cut] Cut013003032012
  Base = -> Cut013003032011
  Tool = -> Box031
FEATURE [Part::Cylinder] Cylinder059  label="Cylinder054"
  Angle = 360
  AttacherType = Attacher::AttachEngine3D
  Height = 10
  Radius = 10
FEATURE [Part::Cylinder] Cylinder060  label="Cylinder055"
  Angle = 360
  AttacherType = Attacher::AttachEngine3D
  Height = 10
  Radius = 7
FEATURE [Part::Box] Box032  label="Cube031"
  AttacherType = Attacher::AttachEngine3D
  Height = 10
  Length = 3
  Placement = pos=(-10,-5,0) rot=(0,0,1;0rad)
  Width = 5
FEATURE [Part::Cut] Cut013003032013
  Base = -> Cylinder059
  Tool = -> Cylinder060
FEATURE [Part::Box] Box033  label="Cube032"
  AttacherType = Attacher::AttachEngine3D
  Height = 10
  Length = 5
  Placement = pos=(0,7,0) rot=(0,0,1;0rad)
  Width = 3
FEATURE [Part::Box] Box034  label="Cube033"
  AttacherType = Attacher::AttachEngine3D
  Height = 10
  Length = 20
  Placement = pos=(-10,-10,0) rot=(0,0,1;0rad)
  Width = 10
FEATURE [Part::Cut] Cut013003032014
  Base = -> Cut013003032013
  Tool = -> Box034
FEATURE [Part::Box] Box035  label="Cube034"
  AttacherType = Attacher::AttachEngine3D
  Height = 10
  Length = 10
  Width = 10
FEATURE [Part::Cut] Cut013003032015
  Base = -> Cut013003032014
  Tool = -> Box035
FEATURE [Part::MultiFuse] Fusion003025020005006  label="corner-cut"
  Shapes = -> [Box032,Cut013003032015,Box033]
FEATURE [Part::Box] Box036  label="Cube035"
  AttacherType = Attacher::AttachEngine3D
  Height = 5
  Length = 8
  Placement = pos=(15,0,35) rot=(0,0,1;0rad)
  Width = 10
FEATURE [Part::Box] Box037  label="Cube036"
  AttacherType = Attacher::AttachEngine3D
  Height = 5
  Length = 8
  Placement = pos=(140,0,23) rot=(0,0,1;0rad)
  Width = 10
FEATURE [Part::Cut] Cut013003032016
  Base = -> Cut013003032009
  Tool = -> Box037
FEATURE [Part::Cut] Cut013003032017
  Base = -> Cut013003032012
  Tool = -> Box036
FEATURE [Part::Box] Box039  label="Cube038"
  AttacherType = Attacher::AttachEngine3D
  Height = 5
  Length = 8
  Placement = pos=(127.37,50,35) rot=(0,0,1;0rad)
  Width = 10
FEATURE [Part::Cut] Cut013003032018
  Base = -> Cut013003032008
  Tool = -> Box039
FEATURE [Part::Box] Box038  label="Cube037"
  AttacherType = Attacher::AttachEngine3D
  Height = 5
  Length = 8
  Placement = pos=(27.63,50,23) rot=(0,0,1;0rad)
  Width = 10
FEATURE [Part::Cut] Cut013003032019
  Base = -> Fusion003025022
  Tool = -> Box038
